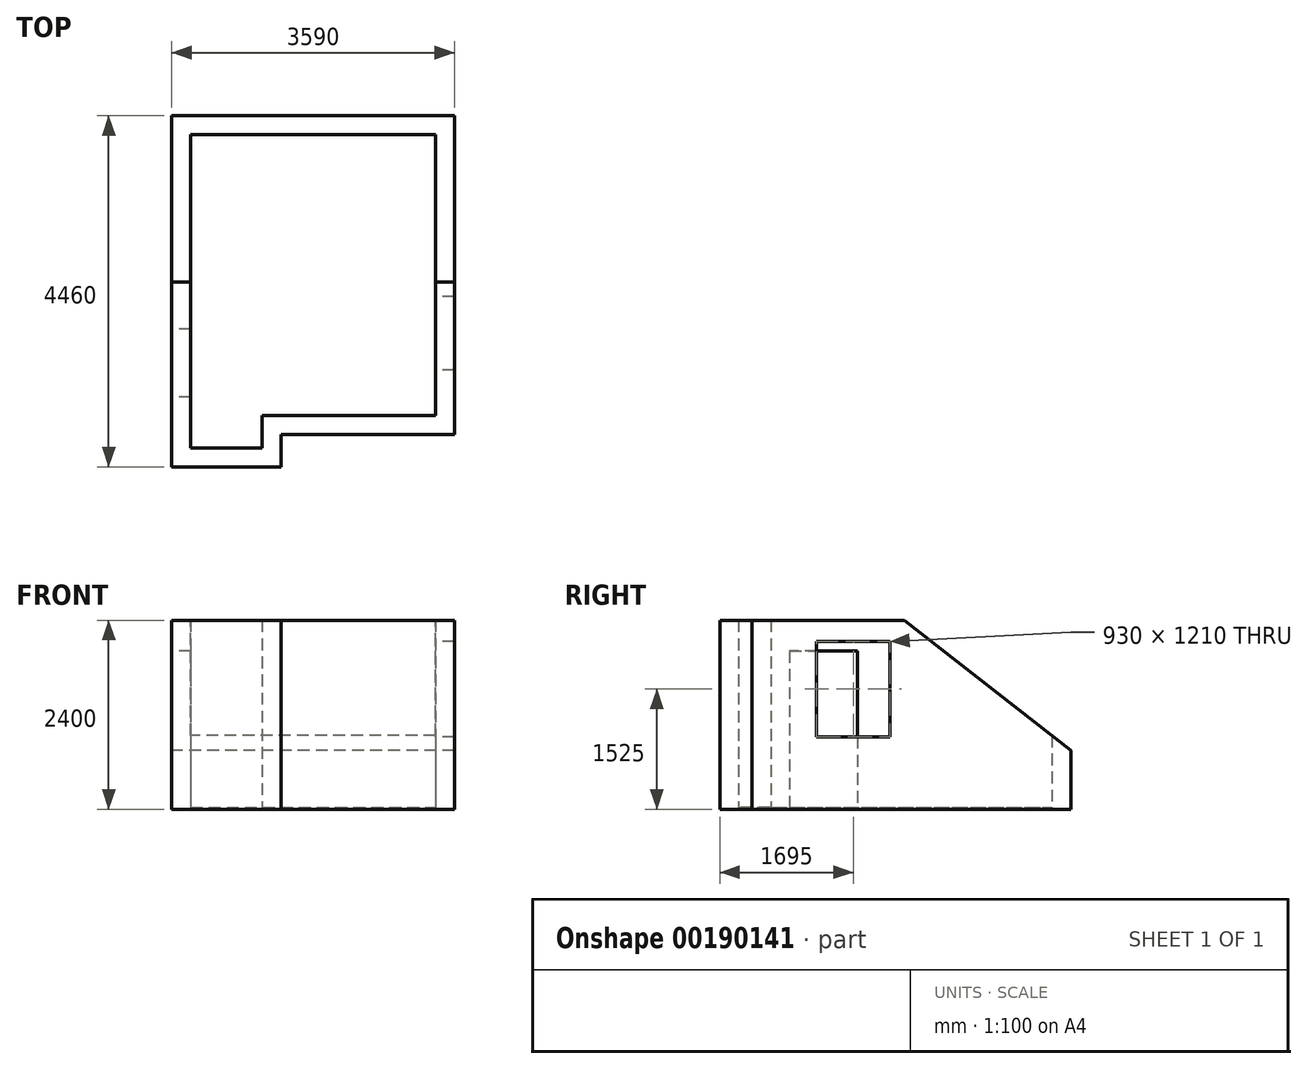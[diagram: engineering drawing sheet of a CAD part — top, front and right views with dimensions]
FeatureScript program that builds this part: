
annotation { "Feature Type Name" : "Feature", "Feature Type Description" : "" }
export const myFeature = defineFeature(function(context is Context, id is Id, definition is map)
    precondition{}
    {
        {
            var Q0;
            Q0=qCreatedBy(makeId("Top.planeOp"),FACE);
            var sketch = newSketch(context, id + "F0", { "sketchPlane" : qUnion([Q0])});
            skPoint(sketch, "E0.middle", {"position": v(0, 0) * mm});
            skLineSegment(sketch, "E1.bottom", {"start": v(910, 0) * mm, "end": v(3110, 0) * mm});
            skLineSegment(sketch, "E1.top", {"start": v(0, 3570) * mm, "end": v(3110, 3570) * mm});
            skLineSegment(sketch, "E1.left", {"start": v(0, 0) * mm, "end": v(0, 3570) * mm});
            skLineSegment(sketch, "E1.right", {"start": v(3110, 0) * mm, "end": v(3110, 3570) * mm});
            skLineSegment(sketch, "E2.top", {"start": v(0, -410) * mm, "end": v(910, -410) * mm});
            skLineSegment(sketch, "E2.left", {"start": v(0, 0) * mm, "end": v(0, -410) * mm});
            skLineSegment(sketch, "E2.right", {"start": v(910, 0) * mm, "end": v(910, -410) * mm});
            skLineSegment(sketch, "E3.0", {"start": v(-240, -650) * mm, "end": v(-240, 3810) * mm});
            skLineSegment(sketch, "E3.2", {"start": v(3350, -240) * mm, "end": v(3350, 3810) * mm});
            skLineSegment(sketch, "E3.3", {"start": v(1150, -240) * mm, "end": v(3350, -240) * mm});
            skLineSegment(sketch, "E3.4", {"start": v(1150, -240) * mm, "end": v(1150, -650) * mm});
            skLineSegment(sketch, "E3.5", {"start": v(-240, 3810) * mm, "end": v(3350, 3810) * mm});
            skLineSegment(sketch, "E3.6", {"start": v(-240, -650) * mm, "end": v(1150, -650) * mm});
            skSolve(sketch);
        }
        {
            var Q0;
            Q0 = qSketchRegion(id + "F0", true);
            extrude(context, id + "F1", {"entities" : qUnion([Q0]), "depth" : 2400 * mm, "offsetDistance" : 25 * mm});
        }
        {
            var Q0;
            Q0=makeQuery(id+"F1.opExtrude","SWEPT_FACE",FACE,{"disambiguationData":[OSD([sQuery(id+"F0.wireOp",EDGE,"E3.0")])]});
            var sketch = newSketch(context, id + "F2", { "sketchPlane" : qUnion([Q0])});
            skLineSegment(sketch, "E4.bottom", {"start": v(-237.1, 0) * mm, "end": v(-1097.1, 0) * mm});
            skLineSegment(sketch, "E4.top", {"start": v(-237.1, 2010) * mm, "end": v(-1097.1, 2010) * mm});
            skLineSegment(sketch, "E4.left", {"start": v(-237.1, 0) * mm, "end": v(-237.1, 2010) * mm});
            skLineSegment(sketch, "E4.right", {"start": v(-1097.1, 0) * mm, "end": v(-1097.1, 2010) * mm});
            skSolve(sketch);
        }
        {
            var Q0;
            Q0 = qSketchRegion(id + "F2", true);
            extrude(context, id + "F3", {"entities" : qUnion([Q0]), "operationType" : NewBodyOperationType.REMOVE, "endBound" : BoundingType.UP_TO_NEXT, "oppositeDirection" : true, "depth" : 25 * mm, "offsetDistance" : 25 * mm});
        }
        {
            var Q0;
            Q0=makeQuery(id+"F1.opExtrude","SWEPT_FACE",FACE,{"disambiguationData":[OSD([sQuery(id+"F0.wireOp",EDGE,"E3.0")])]});
            var sketch = newSketch(context, id + "F4", { "sketchPlane" : qUnion([Q0])});
            skLineSegment(sketch, "E5", {"start": v(-3810, 750) * mm, "end": v(-1698.1, 2400) * mm});
            skLineSegment(sketch, "E6", {"start": v(-1698.1, 2400) * mm, "end": v(-3810, 2400) * mm});
            skLineSegment(sketch, "E7", {"start": v(-3810, 2400) * mm, "end": v(-3810, 750) * mm});
            skSolve(sketch);
        }
        {
            var Q0;
            Q0 = qSketchRegion(id + "F4", true);
            extrude(context, id + "F5", {"entities" : qUnion([Q0]), "operationType" : NewBodyOperationType.REMOVE, "endBound" : BoundingType.THROUGH_ALL, "oppositeDirection" : true, "depth" : 25 * mm, "offsetDistance" : 25 * mm});
        }
        {
            var Q0;
            Q0=makeQuery(id+"F1.opExtrude","SWEPT_FACE",FACE,{"disambiguationData":[OSD([sQuery(id+"F0.wireOp",EDGE,"E1.right")])]});
            var sketch = newSketch(context, id + "F6", { "sketchPlane" : qUnion([Q0])});
            skLineSegment(sketch, "E8.bottom", {"start": v(-580, 920) * mm, "end": v(-1510, 920) * mm});
            skLineSegment(sketch, "E8.top", {"start": v(-580, 2130) * mm, "end": v(-1510, 2130) * mm});
            skLineSegment(sketch, "E8.left", {"start": v(-580, 920) * mm, "end": v(-580, 2130) * mm});
            skLineSegment(sketch, "E8.right", {"start": v(-1510, 920) * mm, "end": v(-1510, 2130) * mm});
            skSolve(sketch);
        }
        {
            var Q0;
            Q0 = qSketchRegion(id + "F6", true);
            extrude(context, id + "F7", {"entities" : qUnion([Q0]), "operationType" : NewBodyOperationType.REMOVE, "endBound" : BoundingType.UP_TO_NEXT, "oppositeDirection" : true, "depth" : 25 * mm, "offsetDistance" : 25 * mm});
        }
        {
            var Q0;
            Q0=makeQuery(id+"F1.opExtrude","CAP_FACE",FACE,{"disambiguationData":[OSD([sQuery(id+"F0.wireOp",EDGE,"E1.bottom"),sQuery(id+"F0.wireOp",EDGE,"E1.top"),sQuery(id+"F0.wireOp",EDGE,"E1.left"),sQuery(id+"F0.wireOp",EDGE,"E1.right"),sQuery(id+"F0.wireOp",EDGE,"E2.top"),sQuery(id+"F0.wireOp",EDGE,"E2.left"),sQuery(id+"F0.wireOp",EDGE,"E2.right"),sQuery(id+"F0.wireOp",EDGE,"E3.0"),sQuery(id+"F0.wireOp",EDGE,"E3.2"),sQuery(id+"F0.wireOp",EDGE,"E3.3"),sQuery(id+"F0.wireOp",EDGE,"E3.4"),sQuery(id+"F0.wireOp",EDGE,"E3.5"),sQuery(id+"F0.wireOp",EDGE,"E3.6")])],"isStart":true});
            var sketch = newSketch(context, id + "F8", { "sketchPlane" : qUnion([Q0])});
            skLineSegment(sketch, "E9.0", {"start": v(0, -1097.1) * mm, "end": v(0, -3570) * mm});
            skLineSegment(sketch, "E10", {"start": v(0, -237.1) * mm, "end": v(0, -1097.1) * mm});
            skLineSegment(sketch, "E11.0", {"start": v(0, -3570) * mm, "end": v(3110, -3570) * mm});
            skLineSegment(sketch, "E12.0", {"start": v(3110, 0) * mm, "end": v(3110, -3570) * mm});
            skLineSegment(sketch, "E13.0", {"start": v(910, 0) * mm, "end": v(3110, 0) * mm});
            skLineSegment(sketch, "E14.0", {"start": v(910, 0) * mm, "end": v(910, 410) * mm});
            skLineSegment(sketch, "E15.0", {"start": v(0, 410) * mm, "end": v(910, 410) * mm});
            skLineSegment(sketch, "E16.0", {"start": v(0, 410) * mm, "end": v(0, -237.1) * mm});
            skSolve(sketch);
        }
        {
            var Q0;
            Q0 = qSketchRegion(id + "F8", true);
            extrude(context, id + "F9", {"entities" : qUnion([Q0]), "oppositeDirection" : true, "depth" : 25 * mm, "offsetDistance" : 25 * mm});
        }
    });
